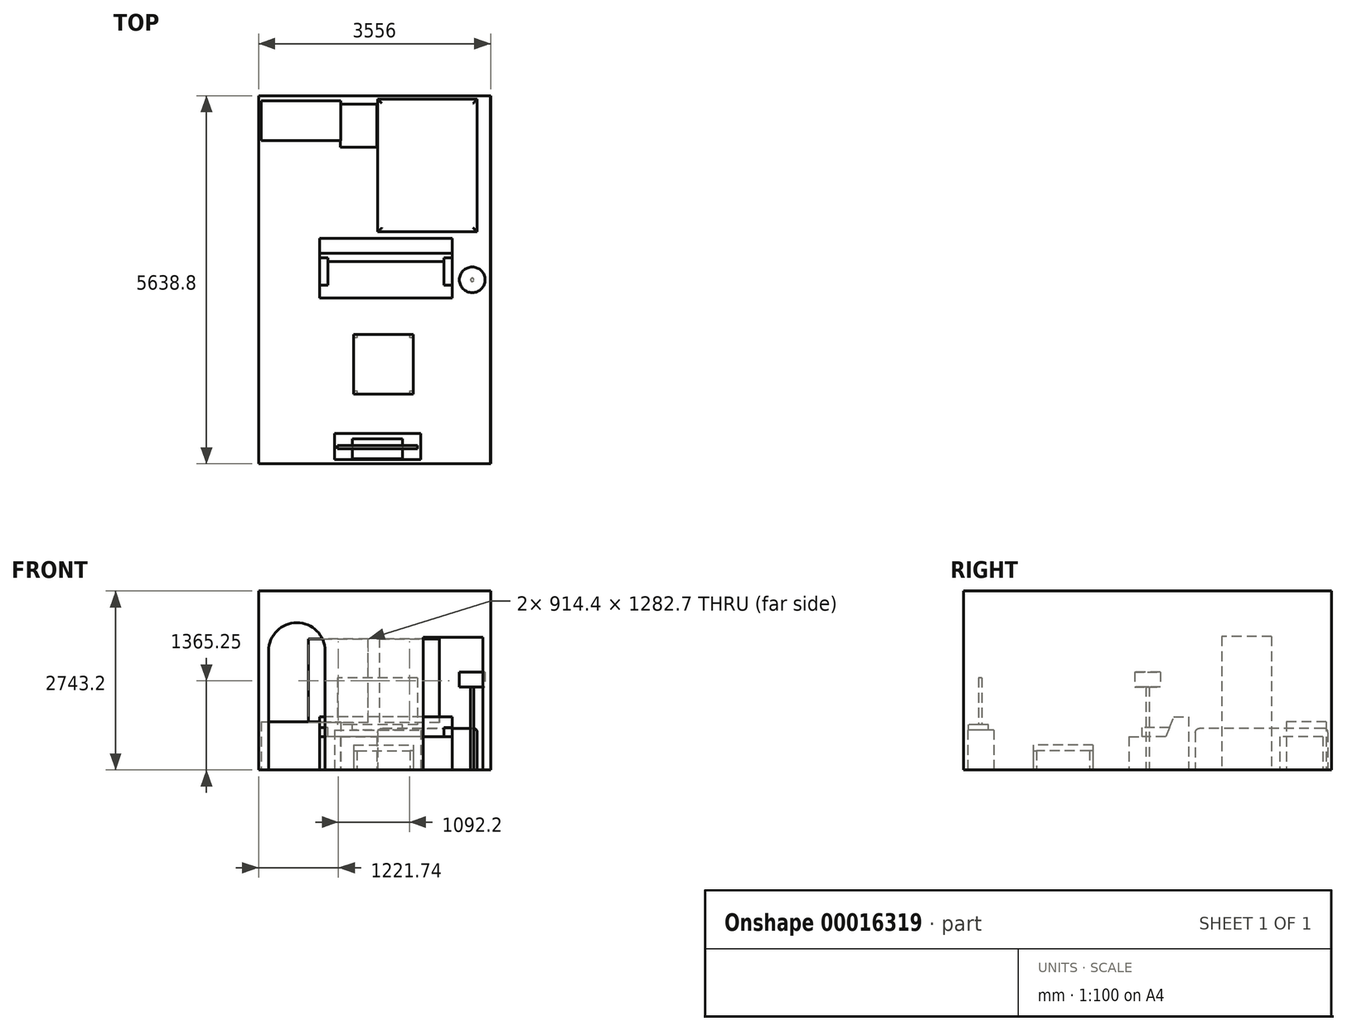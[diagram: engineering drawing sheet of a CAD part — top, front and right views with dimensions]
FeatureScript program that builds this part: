
annotation { "Feature Type Name" : "Feature", "Feature Type Description" : "" }
export const myFeature = defineFeature(function(context is Context, id is Id, definition is map)
    precondition{}
    {
        {
            var Q0;
            Q0=qCreatedBy(makeId("Top.planeOp"),FACE);
            var sketch = newSketch(context, id + "F0", { "sketchPlane" : qUnion([Q0])});
            skLineSegment(sketch, "E0", {"start": v(0, 0) * mm, "end": v(3556, 0) * mm});
            skLineSegment(sketch, "E1", {"start": v(3556, 0) * mm, "end": v(3556, 5638.8) * mm});
            skLineSegment(sketch, "E2", {"start": v(3556, 5638.8) * mm, "end": v(0, 5638.8) * mm});
            skLineSegment(sketch, "E3", {"start": v(0, 5638.8) * mm, "end": v(0, 0) * mm});
            skSolve(sketch);
        }
        {
            var Q0;
            Q0 = qSketchRegion(id + "F0", true);
            extrude(context, id + "F1", {"entities" : qUnion([Q0]), "depth" : 2743.2 * mm});
        }
        {
            var Q0;
            Q0=makeQuery(id+"F1.opExtrude","CAP_FACE",FACE,{"disambiguationData":[OSD([sQuery(id+"F0.wireOp",EDGE,"E0"),sQuery(id+"F0.wireOp",EDGE,"E1"),sQuery(id+"F0.wireOp",EDGE,"E2"),sQuery(id+"F0.wireOp",EDGE,"E3")])],"isStart":false});
            var sketch = newSketch(context, id + "F2", { "sketchPlane" : qUnion([Q0])});
            skLineSegment(sketch, "E4.bottom", {"start": v(2.54, 5636.26) * mm, "end": v(3553.46, 5636.26) * mm});
            skLineSegment(sketch, "E4.top", {"start": v(2.54, 2.54) * mm, "end": v(3553.46, 2.54) * mm});
            skLineSegment(sketch, "E4.left", {"start": v(2.54, 5636.26) * mm, "end": v(2.54, 2.54) * mm});
            skLineSegment(sketch, "E4.right", {"start": v(3553.46, 5636.26) * mm, "end": v(3553.46, 2.54) * mm});
            skSolve(sketch);
        }
        {
            var Q0;
            Q0 = qSketchRegion(id + "F2", true);
            extrude(context, id + "F3", {"entities" : qUnion([Q0]), "operationType" : NewBodyOperationType.REMOVE, "oppositeDirection" : true, "depth" : 2740.66 * mm});
        }
        {
            var Q0;
            Q0=makeQuery(id+"F3.boolean.opBoolean","COPY",FACE,{"derivedFrom":makeQuery(id+"F3.opExtrude","SWEPT_FACE",FACE,{"disambiguationData":[OSD([sQuery(id+"F2.wireOp",EDGE,"E4.top")])]})});
            var sketch = newSketch(context, id + "F4", { "sketchPlane" : qUnion([Q0])});
            skLineSegment(sketch, "E5", {"start": v(-1018.54, 2.54) * mm, "end": v(-1018.54, 1825) * mm});
            skLineSegment(sketch, "E6", {"start": v(-154.94, 2.54) * mm, "end": v(-154.94, 1824.99) * mm});
            skArc(sketch, "E7", {"start": v(-1018.54, 1824.99) * mm, "mid": v(-586.74, 2256.79) * mm, "end": v(-154.94, 1824.99) * mm});
            skLineSegment(sketch, "E8", {"start": v(-3439.16, 0) * mm, "end": v(-3439.16, 2032) * mm});
            skLineSegment(sketch, "E9", {"start": v(-3439.16, 2032) * mm, "end": v(-2524.76, 2032) * mm});
            skLineSegment(sketch, "E10", {"start": v(-2524.76, 2032) * mm, "end": v(-2524.76, 0) * mm});
            skLineSegment(sketch, "E11", {"start": v(-2524.76, 0) * mm, "end": v(-3439.16, 0) * mm});
            skLineSegment(sketch, "E12", {"start": v(-1018.54, 2.54) * mm, "end": v(-154.94, 2.54) * mm});
            skSolve(sketch);
        }
        {
            var Q0;
            Q0 = qSketchRegion(id + "F4", true);
            var Q1;
            Q1=makeQuery(id+"F1.opExtrude","SWEPT_FACE",FACE,{"disambiguationData":[OSD([sQuery(id+"F0.wireOp",EDGE,"E0")])]});
            extrude(context, id + "F5", {"entities" : qUnion([Q0]), "operationType" : NewBodyOperationType.REMOVE, "endBound" : BoundingType.UP_TO_SURFACE, "oppositeDirection" : true, "endBoundEntityFace" : qUnion([Q1]), "depth" : 25.4 * mm});
        }
        {
            var Q0;
            Q0=makeQuery(id+"F3.boolean.opBoolean","COPY",FACE,{"derivedFrom":makeQuery(id+"F3.opExtrude","SWEPT_FACE",FACE,{"disambiguationData":[OSD([sQuery(id+"F2.wireOp",EDGE,"E4.left")])]})});
            var sketch = newSketch(context, id + "F6", { "sketchPlane" : qUnion([Q0])});
            skLineSegment(sketch, "E13.bottom", {"start": v(3959.86, 2.54) * mm, "end": v(4721.86, 2.54) * mm});
            skLineSegment(sketch, "E13.top", {"start": v(3959.86, 2047.24) * mm, "end": v(4721.86, 2047.24) * mm});
            skLineSegment(sketch, "E13.left", {"start": v(3959.86, 2.54) * mm, "end": v(3959.86, 2047.24) * mm});
            skLineSegment(sketch, "E13.right", {"start": v(4721.86, 2.54) * mm, "end": v(4721.86, 2047.24) * mm});
            skSolve(sketch);
        }
        {
            var Q0;
            Q0 = qSketchRegion(id + "F6", true);
            var Q1;
            Q1=makeQuery(id+"F1.opExtrude","SWEPT_FACE",FACE,{"disambiguationData":[OSD([sQuery(id+"F0.wireOp",EDGE,"E3")])]});
            extrude(context, id + "F7", {"entities" : qUnion([Q0]), "operationType" : NewBodyOperationType.REMOVE, "endBound" : BoundingType.UP_TO_SURFACE, "oppositeDirection" : true, "endBoundEntityFace" : qUnion([Q1]), "depth" : 25.4 * mm});
        }
        {
            var Q0;
            Q0=makeQuery(id+"F3.boolean.opBoolean","COPY",FACE,{"derivedFrom":makeQuery(id+"F3.opExtrude","SWEPT_FACE",FACE,{"disambiguationData":[OSD([sQuery(id+"F2.wireOp",EDGE,"E4.bottom")])]})});
            var sketch = newSketch(context, id + "F8", { "sketchPlane" : qUnion([Q0])});
            skLineSegment(sketch, "E14.bottom", {"start": v(764.54, 2006.6) * mm, "end": v(1678.94, 2006.6) * mm});
            skLineSegment(sketch, "E14.top", {"start": v(764.54, 723.9) * mm, "end": v(1678.94, 723.9) * mm});
            skLineSegment(sketch, "E14.left", {"start": v(764.54, 2006.6) * mm, "end": v(764.54, 723.9) * mm});
            skLineSegment(sketch, "E14.right", {"start": v(1678.94, 2006.6) * mm, "end": v(1678.94, 723.9) * mm});
            skLineSegment(sketch, "E15.bottom", {"start": v(1856.74, 2006.6) * mm, "end": v(2771.14, 2006.6) * mm});
            skLineSegment(sketch, "E15.top", {"start": v(1856.74, 723.9) * mm, "end": v(2771.14, 723.9) * mm});
            skLineSegment(sketch, "E15.left", {"start": v(1856.74, 2006.6) * mm, "end": v(1856.74, 723.9) * mm});
            skLineSegment(sketch, "E15.right", {"start": v(2771.14, 2006.6) * mm, "end": v(2771.14, 723.9) * mm});
            skSolve(sketch);
        }
        {
            var Q0;
            Q0 = qSketchRegion(id + "F8", true);
            var Q1;
            Q1=makeQuery(id+"F1.opExtrude","SWEPT_FACE",FACE,{"disambiguationData":[OSD([sQuery(id+"F0.wireOp",EDGE,"E2")])]});
            extrude(context, id + "F9", {"entities" : qUnion([Q0]), "operationType" : NewBodyOperationType.REMOVE, "endBound" : BoundingType.UP_TO_SURFACE, "oppositeDirection" : true, "endBoundEntityFace" : qUnion([Q1]), "depth" : 25.4 * mm});
        }
        {
            var Q0;
            Q0=makeQuery(id+"F5.boolean.opBoolean","MERGE",FACE,{"derivedFrom":[makeQuery(id+"F3.boolean.opBoolean","COPY",FACE,{"derivedFrom":makeQuery(id+"F3.opExtrude","CAP_FACE",FACE,{"disambiguationData":[OSD([sQuery(id+"F2.wireOp",EDGE,"E4.bottom"),sQuery(id+"F2.wireOp",EDGE,"E4.top"),sQuery(id+"F2.wireOp",EDGE,"E4.left"),sQuery(id+"F2.wireOp",EDGE,"E4.right")])],"isStart":false})}),makeQuery(id+"F5.opExtrude","SWEPT_FACE",FACE,{"disambiguationData":[OSD([sQuery(id+"F4.wireOp",EDGE,"E12")])]})]});
            var sketch = newSketch(context, id + "F10", { "sketchPlane" : qUnion([Q0])});
            skLineSegment(sketch, "E16", {"start": v(3350.26, 5585.46) * mm, "end": v(3350.26, 3553.46) * mm});
            skLineSegment(sketch, "E17", {"start": v(3350.26, 3553.46) * mm, "end": v(1826.26, 3553.46) * mm});
            skLineSegment(sketch, "E18", {"start": v(1826.26, 3553.46) * mm, "end": v(1826.26, 5585.46) * mm});
            skLineSegment(sketch, "E19", {"start": v(1826.26, 5585.46) * mm, "end": v(3350.26, 5585.46) * mm});
            skSolve(sketch);
        }
        {
            var Q0;
            Q0 = qSketchRegion(id + "F10", true);
            extrude(context, id + "F11", {"entities" : qUnion([Q0]), "depth" : 635 * mm});
        }
        {
            var Q0;
            Q0=makeQuery(id+"F11.opExtrude","CAP_EDGE",EDGE,{"disambiguationData":[OSD([sQuery(id+"F10.wireOp",EDGE,"E18")])],"isStart":false});
            var Q1;
            Q1=makeQuery(id+"F11.opExtrude","CAP_EDGE",EDGE,{"disambiguationData":[OSD([sQuery(id+"F10.wireOp",EDGE,"E17")])],"isStart":false});
            var Q2;
            Q2=makeQuery(id+"F11.opExtrude","CAP_EDGE",EDGE,{"disambiguationData":[OSD([sQuery(id+"F10.wireOp",EDGE,"E16")])],"isStart":false});
            var Q3;
            Q3=makeQuery(id+"F11.opExtrude","CAP_EDGE",EDGE,{"disambiguationData":[OSD([sQuery(id+"F10.wireOp",EDGE,"E19")])],"isStart":false});
            fillet(context, id + "F12", {"entities" : qUnion([Q0, Q1, Q2, Q3]), "radius" : 63.5 * mm, "tangentPropagation" : true, "allowEdgeOverflow" : false});
        }
        {
            var Q0;
            Q0=makeQuery(id+"F5.boolean.opBoolean","MERGE",FACE,{"derivedFrom":[makeQuery(id+"F3.boolean.opBoolean","COPY",FACE,{"derivedFrom":makeQuery(id+"F3.opExtrude","CAP_FACE",FACE,{"disambiguationData":[OSD([sQuery(id+"F2.wireOp",EDGE,"E4.bottom"),sQuery(id+"F2.wireOp",EDGE,"E4.top"),sQuery(id+"F2.wireOp",EDGE,"E4.left"),sQuery(id+"F2.wireOp",EDGE,"E4.right")])],"isStart":false})}),makeQuery(id+"F5.opExtrude","SWEPT_FACE",FACE,{"disambiguationData":[OSD([sQuery(id+"F4.wireOp",EDGE,"E12")])]})]});
            var sketch = newSketch(context, id + "F13", { "sketchPlane" : qUnion([Q0])});
            skLineSegment(sketch, "E20.bottom", {"start": v(1254.76, 5509.26) * mm, "end": v(1813.56, 5509.26) * mm});
            skLineSegment(sketch, "E20.top", {"start": v(1254.76, 4848.86) * mm, "end": v(1813.56, 4848.86) * mm});
            skLineSegment(sketch, "E20.left", {"start": v(1254.76, 5509.26) * mm, "end": v(1254.76, 4848.86) * mm});
            skLineSegment(sketch, "E20.right", {"start": v(1813.56, 5509.26) * mm, "end": v(1813.56, 4848.86) * mm});
            skSolve(sketch);
        }
        {
            var Q0;
            Q0 = qSketchRegion(id + "F13", true);
            extrude(context, id + "F14", {"entities" : qUnion([Q0]), "depth" : 508 * mm});
        }
        {
            var Q0;
            Q0=makeQuery(id+"F5.boolean.opBoolean","MERGE",FACE,{"derivedFrom":[makeQuery(id+"F3.boolean.opBoolean","COPY",FACE,{"derivedFrom":makeQuery(id+"F3.opExtrude","CAP_FACE",FACE,{"disambiguationData":[OSD([sQuery(id+"F2.wireOp",EDGE,"E4.bottom"),sQuery(id+"F2.wireOp",EDGE,"E4.top"),sQuery(id+"F2.wireOp",EDGE,"E4.left"),sQuery(id+"F2.wireOp",EDGE,"E4.right")])],"isStart":false})}),makeQuery(id+"F5.opExtrude","SWEPT_FACE",FACE,{"disambiguationData":[OSD([sQuery(id+"F4.wireOp",EDGE,"E12")])]})]});
            var sketch = newSketch(context, id + "F15", { "sketchPlane" : qUnion([Q0])});
            skLineSegment(sketch, "E21.bottom", {"start": v(40.64, 5560.06) * mm, "end": v(1259.84, 5560.06) * mm});
            skLineSegment(sketch, "E21.top", {"start": v(40.64, 4950.46) * mm, "end": v(1259.84, 4950.46) * mm});
            skLineSegment(sketch, "E21.left", {"start": v(40.64, 5560.06) * mm, "end": v(40.64, 4950.46) * mm});
            skLineSegment(sketch, "E21.right", {"start": v(1259.84, 5560.06) * mm, "end": v(1259.84, 4950.46) * mm});
            skSolve(sketch);
        }
        {
            var Q0;
            Q0 = qSketchRegion(id + "F15", true);
            extrude(context, id + "F16", {"entities" : qUnion([Q0]), "depth" : 736.6 * mm});
        }
        {
            var Q0;
            Q0=makeQuery(id+"F7.boolean.opBoolean","MERGE",FACE,{"derivedFrom":[makeQuery(id+"F5.boolean.opBoolean","MERGE",FACE,{"derivedFrom":[makeQuery(id+"F3.boolean.opBoolean","COPY",FACE,{"derivedFrom":makeQuery(id+"F3.opExtrude","CAP_FACE",FACE,{"disambiguationData":[OSD([sQuery(id+"F2.wireOp",EDGE,"E4.bottom"),sQuery(id+"F2.wireOp",EDGE,"E4.top"),sQuery(id+"F2.wireOp",EDGE,"E4.left"),sQuery(id+"F2.wireOp",EDGE,"E4.right")])],"isStart":false})}),makeQuery(id+"F5.opExtrude","SWEPT_FACE",FACE,{"disambiguationData":[OSD([sQuery(id+"F4.wireOp",EDGE,"E12")])]})]}),makeQuery(id+"F7.opExtrude","SWEPT_FACE",FACE,{"disambiguationData":[OSD([sQuery(id+"F6.wireOp",EDGE,"E13.bottom")])]})]});
            var sketch = newSketch(context, id + "F17", { "sketchPlane" : qUnion([Q0])});
            skLineSegment(sketch, "E22.bottom", {"start": v(2969.26, 2537.46) * mm, "end": v(937.26, 2537.46) * mm});
            skLineSegment(sketch, "E22.top", {"start": v(2969.26, 3451.86) * mm, "end": v(937.26, 3451.86) * mm});
            skLineSegment(sketch, "E22.left", {"start": v(2969.26, 2537.46) * mm, "end": v(2969.26, 3451.86) * mm});
            skLineSegment(sketch, "E22.right", {"start": v(937.26, 2537.46) * mm, "end": v(937.26, 3451.86) * mm});
            skSolve(sketch);
        }
        {
            var Q0;
            Q0 = qSketchRegion(id + "F17", true);
            extrude(context, id + "F18", {"entities" : qUnion([Q0]), "depth" : 812.8 * mm});
        }
        {
            var Q0;
            Q0=makeQuery(id+"F7.boolean.opBoolean","MERGE",FACE,{"derivedFrom":[makeQuery(id+"F5.boolean.opBoolean","MERGE",FACE,{"derivedFrom":[makeQuery(id+"F3.boolean.opBoolean","COPY",FACE,{"derivedFrom":makeQuery(id+"F3.opExtrude","CAP_FACE",FACE,{"disambiguationData":[OSD([sQuery(id+"F2.wireOp",EDGE,"E4.bottom"),sQuery(id+"F2.wireOp",EDGE,"E4.top"),sQuery(id+"F2.wireOp",EDGE,"E4.left"),sQuery(id+"F2.wireOp",EDGE,"E4.right")])],"isStart":false})}),makeQuery(id+"F5.opExtrude","SWEPT_FACE",FACE,{"disambiguationData":[OSD([sQuery(id+"F4.wireOp",EDGE,"E12")])]})]}),makeQuery(id+"F7.opExtrude","SWEPT_FACE",FACE,{"disambiguationData":[OSD([sQuery(id+"F6.wireOp",EDGE,"E13.bottom")])]})]});
            var sketch = newSketch(context, id + "F19", { "sketchPlane" : qUnion([Q0])});
            skLineSegment(sketch, "E23.bottom", {"start": v(1457.96, 1983.74) * mm, "end": v(2372.36, 1983.74) * mm});
            skLineSegment(sketch, "E23.top", {"start": v(1457.96, 1069.34) * mm, "end": v(2372.36, 1069.34) * mm});
            skLineSegment(sketch, "E23.left", {"start": v(1457.96, 1983.74) * mm, "end": v(1457.96, 1069.34) * mm});
            skLineSegment(sketch, "E23.right", {"start": v(2372.36, 1983.74) * mm, "end": v(2372.36, 1069.34) * mm});
            skSolve(sketch);
        }
        {
            var Q0;
            Q0 = qSketchRegion(id + "F19", true);
            extrude(context, id + "F20", {"entities" : qUnion([Q0]), "depth" : 381 * mm});
        }
        {
            var Q0;
            Q0=makeQuery(id+"F20.opExtrude","CAP_FACE",FACE,{"disambiguationData":[OSD([sQuery(id+"F19.wireOp",EDGE,"E23.bottom"),sQuery(id+"F19.wireOp",EDGE,"E23.top"),sQuery(id+"F19.wireOp",EDGE,"E23.left"),sQuery(id+"F19.wireOp",EDGE,"E23.right")])],"isStart":true});
            var sketch = newSketch(context, id + "F21", { "sketchPlane" : qUnion([Q0])});
            skLineSegment(sketch, "E24", {"start": v(1508.76, -1983.74) * mm, "end": v(1508.76, -1932.94) * mm});
            skLineSegment(sketch, "E25", {"start": v(1508.76, -1932.94) * mm, "end": v(1457.96, -1932.94) * mm});
            skLineSegment(sketch, "E26", {"start": v(1457.96, -1932.94) * mm, "end": v(1457.96, -1120.14) * mm});
            skLineSegment(sketch, "E27", {"start": v(1457.96, -1120.14) * mm, "end": v(1508.76, -1120.14) * mm});
            skLineSegment(sketch, "E28", {"start": v(1508.76, -1120.14) * mm, "end": v(1508.76, -1069.34) * mm});
            skLineSegment(sketch, "E29", {"start": v(1508.76, -1069.34) * mm, "end": v(2321.56, -1069.34) * mm});
            skLineSegment(sketch, "E30", {"start": v(2321.56, -1069.34) * mm, "end": v(2321.56, -1120.14) * mm});
            skLineSegment(sketch, "E31", {"start": v(2321.56, -1120.14) * mm, "end": v(2372.36, -1120.14) * mm});
            skLineSegment(sketch, "E32", {"start": v(2372.36, -1120.14) * mm, "end": v(2372.36, -1932.94) * mm});
            skLineSegment(sketch, "E33", {"start": v(2372.36, -1932.94) * mm, "end": v(2321.56, -1932.94) * mm});
            skLineSegment(sketch, "E34", {"start": v(2321.56, -1932.94) * mm, "end": v(2321.56, -1983.74) * mm});
            skLineSegment(sketch, "E35", {"start": v(2321.56, -1983.74) * mm, "end": v(1508.76, -1983.74) * mm});
            skSolve(sketch);
        }
        {
            var Q0;
            Q0=makeQuery(id+"F21.imprint","IMPRINT",FACE,{"disambiguationData":[TD([[makeQuery(id+"F21.imprint","IMPRINT",EDGE,{"derivedFrom":sQuery(id+"F21.wireOp",EDGE,"E24")}),-1.0]])]});
            extrude(context, id + "F22", {"entities" : qUnion([Q0]), "operationType" : NewBodyOperationType.REMOVE, "oppositeDirection" : true, "depth" : 292.1 * mm});
        }
        {
            var Q0;
            Q0=makeQuery(id+"F18.opExtrude","SWEPT_FACE",FACE,{"disambiguationData":[OSD([sQuery(id+"F17.wireOp",EDGE,"E22.right")])]});
            var sketch = newSketch(context, id + "F23", { "sketchPlane" : qUnion([Q0])});
            skLineSegment(sketch, "E36", {"start": v(-3223.26, 815.34) * mm, "end": v(-3156.62, 650.24) * mm});
            skLineSegment(sketch, "E37", {"start": v(-2537.46, 510.54) * mm, "end": v(-2537.46, 815.34) * mm});
            skLineSegment(sketch, "E38", {"start": v(-2537.46, 815.34) * mm, "end": v(-3223.26, 815.34) * mm});
            skLineSegment(sketch, "E39", {"start": v(-3156.62, 650.24) * mm, "end": v(-2737.52, 650.24) * mm});
            skLineSegment(sketch, "E40", {"start": v(-2737.52, 650.24) * mm, "end": v(-2737.52, 510.54) * mm});
            skLineSegment(sketch, "E41", {"start": v(-2737.52, 510.54) * mm, "end": v(-2537.46, 510.54) * mm});
            skPoint(sketch, "E42", {"position": v(-3451.86, 815.34) * mm});
            skSolve(sketch);
        }
        {
            var Q0;
            Q0=makeQuery(id+"F23.imprint","IMPRINT",FACE,{"disambiguationData":[TD([[makeQuery(id+"F23.imprint","IMPRINT",EDGE,{"derivedFrom":sQuery(id+"F23.wireOp",EDGE,"E36")}),1.0]])]});
            var Q1;
            Q1=makeQuery(id+"F18.opExtrude","SWEPT_FACE",FACE,{"disambiguationData":[OSD([sQuery(id+"F17.wireOp",EDGE,"E22.left")])]});
            extrude(context, id + "F24", {"entities" : qUnion([Q0]), "operationType" : NewBodyOperationType.REMOVE, "endBound" : BoundingType.UP_TO_SURFACE, "oppositeDirection" : true, "endBoundEntityFace" : qUnion([Q1]), "depth" : 25.4 * mm});
        }
        {
            var Q0;
            Q0=makeQuery(id+"F18.opExtrude","SWEPT_FACE",FACE,{"disambiguationData":[OSD([sQuery(id+"F17.wireOp",EDGE,"E22.right")])]});
            var sketch = newSketch(context, id + "F25", { "sketchPlane" : qUnion([Q0])});
            skLineSegment(sketch, "E43", {"start": v(-2537.46, 510.54) * mm, "end": v(-3100.23, 510.54) * mm});
            skLineSegment(sketch, "E44", {"start": v(-3223.26, 815.34) * mm, "end": v(-3156.62, 650.24) * mm, "construction": true});
            skLineSegment(sketch, "E45", {"start": v(-3156.62, 650.24) * mm, "end": v(-3100.23, 510.54) * mm});
            skLineSegment(sketch, "E46", {"start": v(-3156.62, 650.24) * mm, "end": v(-2537.46, 650.24) * mm});
            skLineSegment(sketch, "E47", {"start": v(-2537.46, 650.24) * mm, "end": v(-2537.46, 510.54) * mm});
            skSolve(sketch);
        }
        {
            var Q0;
            Q0 = qSketchRegion(id + "F25", true);
            extrude(context, id + "F26", {"entities" : qUnion([Q0]), "operationType" : NewBodyOperationType.REMOVE, "oppositeDirection" : true, "depth" : 1905 * mm, "hasSecondDirection" : true, "secondDirectionOppositeDirection" : true, "secondDirectionDepth" : 127 * mm});
        }
        {
            var Q0;
            Q0=makeQuery(id+"F3.boolean.opBoolean","COPY",FACE,{"derivedFrom":makeQuery(id+"F3.opExtrude","SWEPT_FACE",FACE,{"disambiguationData":[OSD([sQuery(id+"F2.wireOp",EDGE,"E4.top")])]})});
            var sketch = newSketch(context, id + "F27", { "sketchPlane" : qUnion([Q0])});
            skLineSegment(sketch, "E48.bottom", {"start": v(-2435.86, 1412.24) * mm, "end": v(-1206.5, 1412.24) * mm});
            skLineSegment(sketch, "E48.top", {"start": v(-2435.86, 693.42) * mm, "end": v(-1206.5, 693.42) * mm});
            skLineSegment(sketch, "E48.left", {"start": v(-2435.86, 1412.24) * mm, "end": v(-2435.86, 693.42) * mm});
            skLineSegment(sketch, "E48.right", {"start": v(-1206.5, 1412.24) * mm, "end": v(-1206.5, 693.42) * mm});
            skSolve(sketch);
        }
        {
            var Q0;
            Q0 = qSketchRegion(id + "F27", true);
            extrude(context, id + "F28", {"entities" : qUnion([Q0]), "depth" : 279.4 * mm, "hasSecondDirection" : true, "secondDirectionOppositeDirection" : false, "secondDirectionDepth" : 228.6 * mm});
        }
        {
            var Q0;
            Q0=makeQuery(id+"F28.opExtrude","SWEPT_FACE",FACE,{"disambiguationData":[OSD([sQuery(id+"F27.wireOp",EDGE,"E48.top")])]});
            var sketch = newSketch(context, id + "F29", { "sketchPlane" : qUnion([Q0])});
            skLineSegment(sketch, "E49.bottom", {"start": v(2203.28, -383.54) * mm, "end": v(1439.08, -383.54) * mm});
            skLineSegment(sketch, "E49.top", {"start": v(2203.28, -76.2) * mm, "end": v(1439.08, -76.2) * mm});
            skLineSegment(sketch, "E49.left", {"start": v(2203.28, -383.54) * mm, "end": v(2203.28, -76.2) * mm});
            skLineSegment(sketch, "E49.right", {"start": v(1439.08, -383.54) * mm, "end": v(1439.08, -76.2) * mm});
            skLineSegment(sketch, "E50", {"start": v(2203.28, -281.94) * mm, "end": v(2435.86, -281.94) * mm, "construction": true});
            skLineSegment(sketch, "E51", {"start": v(1439.08, -281.94) * mm, "end": v(1206.5, -281.94) * mm, "construction": true});
            skSolve(sketch);
        }
        {
            var Q0;
            {var subQ5=sQuery(id+"F29.wireOp",EDGE,"E49.bottom");Q0=makeQuery(id+"F29.imprint","IMPRINT",FACE,{"disambiguationData":[TD([[makeQuery(id+"F29.imprint","IMPRINT",EDGE,{"derivedFrom":subQ5}),-1.0]])]});}
            var Q1;
            {var subQ0=sQuery(id+"F27.wireOp",EDGE,"E48.top");var subQ1=makeQuery(id+"F28.opExtrude","CAP_EDGE",EDGE,{"disambiguationData":[OSD([subQ0])],"isStart":false});var subQ4=sQuery(id+"F29.wireOp",EDGE,"E49.left");var subQ5=makeQuery(id+"F29.imprint","INTERSECT",VERTEX,{"derivedFrom":[subQ1,subQ4]});Q1=makeQuery(id+"F29.imprint","IMPRINT",FACE,{"disambiguationData":[TD([[makeQuery(id+"F29.imprint","IMPRINT",EDGE,{"disambiguationData":[TD([[subQ5,-1.0]])],"derivedFrom":subQ4}),1.0]])]});}
            var Q2;
            {var subQ5=sQuery(id+"F29.wireOp",EDGE,"E49.top");Q2=makeQuery(id+"F29.imprint","IMPRINT",FACE,{"disambiguationData":[TD([[makeQuery(id+"F29.imprint","IMPRINT",EDGE,{"derivedFrom":subQ5}),1.0]])]});}
            extrude(context, id + "F30", {"entities" : qUnion([Q0, Q1, Q2]), "operationType" : NewBodyOperationType.ADD, "depth" : 81.28 * mm});
        }
        {
            var Q0;
            Q0=makeQuery(id+"F7.boolean.opBoolean","MERGE",FACE,{"derivedFrom":[makeQuery(id+"F5.boolean.opBoolean","MERGE",FACE,{"derivedFrom":[makeQuery(id+"F3.boolean.opBoolean","COPY",FACE,{"derivedFrom":makeQuery(id+"F3.opExtrude","CAP_FACE",FACE,{"disambiguationData":[OSD([sQuery(id+"F2.wireOp",EDGE,"E4.bottom"),sQuery(id+"F2.wireOp",EDGE,"E4.top"),sQuery(id+"F2.wireOp",EDGE,"E4.left"),sQuery(id+"F2.wireOp",EDGE,"E4.right")])],"isStart":false})}),makeQuery(id+"F5.opExtrude","SWEPT_FACE",FACE,{"disambiguationData":[OSD([sQuery(id+"F4.wireOp",EDGE,"E12")])]})]}),makeQuery(id+"F7.opExtrude","SWEPT_FACE",FACE,{"disambiguationData":[OSD([sQuery(id+"F6.wireOp",EDGE,"E13.bottom")])]})]});
            var sketch = newSketch(context, id + "F31", { "sketchPlane" : qUnion([Q0])});
            skCircle(sketch, "E52", {"center": v(3273.9, 2818.9) * mm, "radius": 25.4 * mm});
            skSolve(sketch);
        }
        {
            var Q0;
            Q0 = qSketchRegion(id + "F31", true);
            extrude(context, id + "F32", {"entities" : qUnion([Q0]), "depth" : 1270 * mm});
        }
        {
            var Q0;
            Q0=makeQuery(id+"F32.opExtrude","CAP_FACE",FACE,{"disambiguationData":[OSD([sQuery(id+"F31.wireOp",EDGE,"E52")])],"isStart":false});
            var sketch = newSketch(context, id + "F33", { "sketchPlane" : qUnion([Q0])});
            skCircle(sketch, "E53", {"center": v(3273.9, 2818.9) * mm, "radius": 196.85 * mm});
            skSolve(sketch);
        }
        {
            var Q0;
            Q0 = qSketchRegion(id + "F33", true);
            extrude(context, id + "F34", {"entities" : qUnion([Q0]), "operationType" : NewBodyOperationType.ADD, "depth" : 228.6 * mm});
        }
        {
            var Q0;
            Q0=makeQuery(id+"F7.boolean.opBoolean","MERGE",FACE,{"derivedFrom":[makeQuery(id+"F5.boolean.opBoolean","MERGE",FACE,{"derivedFrom":[makeQuery(id+"F3.boolean.opBoolean","COPY",FACE,{"derivedFrom":makeQuery(id+"F3.opExtrude","CAP_FACE",FACE,{"disambiguationData":[OSD([sQuery(id+"F2.wireOp",EDGE,"E4.bottom"),sQuery(id+"F2.wireOp",EDGE,"E4.top"),sQuery(id+"F2.wireOp",EDGE,"E4.left"),sQuery(id+"F2.wireOp",EDGE,"E4.right")])],"isStart":false})}),makeQuery(id+"F5.opExtrude","SWEPT_FACE",FACE,{"disambiguationData":[OSD([sQuery(id+"F4.wireOp",EDGE,"E12")])]})]}),makeQuery(id+"F7.opExtrude","SWEPT_FACE",FACE,{"disambiguationData":[OSD([sQuery(id+"F6.wireOp",EDGE,"E13.bottom")])]})]});
            var sketch = newSketch(context, id + "F35", { "sketchPlane" : qUnion([Q0])});
            skLineSegment(sketch, "E54.rect.bottom", {"start": v(1160.78, 466.1) * mm, "end": v(2481.58, 466.1) * mm});
            skLineSegment(sketch, "E54.rect.top", {"start": v(1160.78, 66.04) * mm, "end": v(2481.58, 66.04) * mm});
            skLineSegment(sketch, "E54.rect.left", {"start": v(1160.78, 466.1) * mm, "end": v(1160.78, 66.04) * mm});
            skLineSegment(sketch, "E54.rect.right", {"start": v(2481.58, 466.1) * mm, "end": v(2481.58, 66.04) * mm});
            skPoint(sketch, "E54.rect.middle", {"position": v(1821.18, 266.06) * mm});
            skLineSegment(sketch, "E55", {"start": v(2524.76, 2.54) * mm, "end": v(2524.76, 310.5) * mm, "construction": true});
            skSolve(sketch);
        }
        {
            var Q0;
            Q0 = qSketchRegion(id + "F35", true);
            extrude(context, id + "F36", {"entities" : qUnion([Q0]), "depth" : 609.6 * mm});
        }
    });
